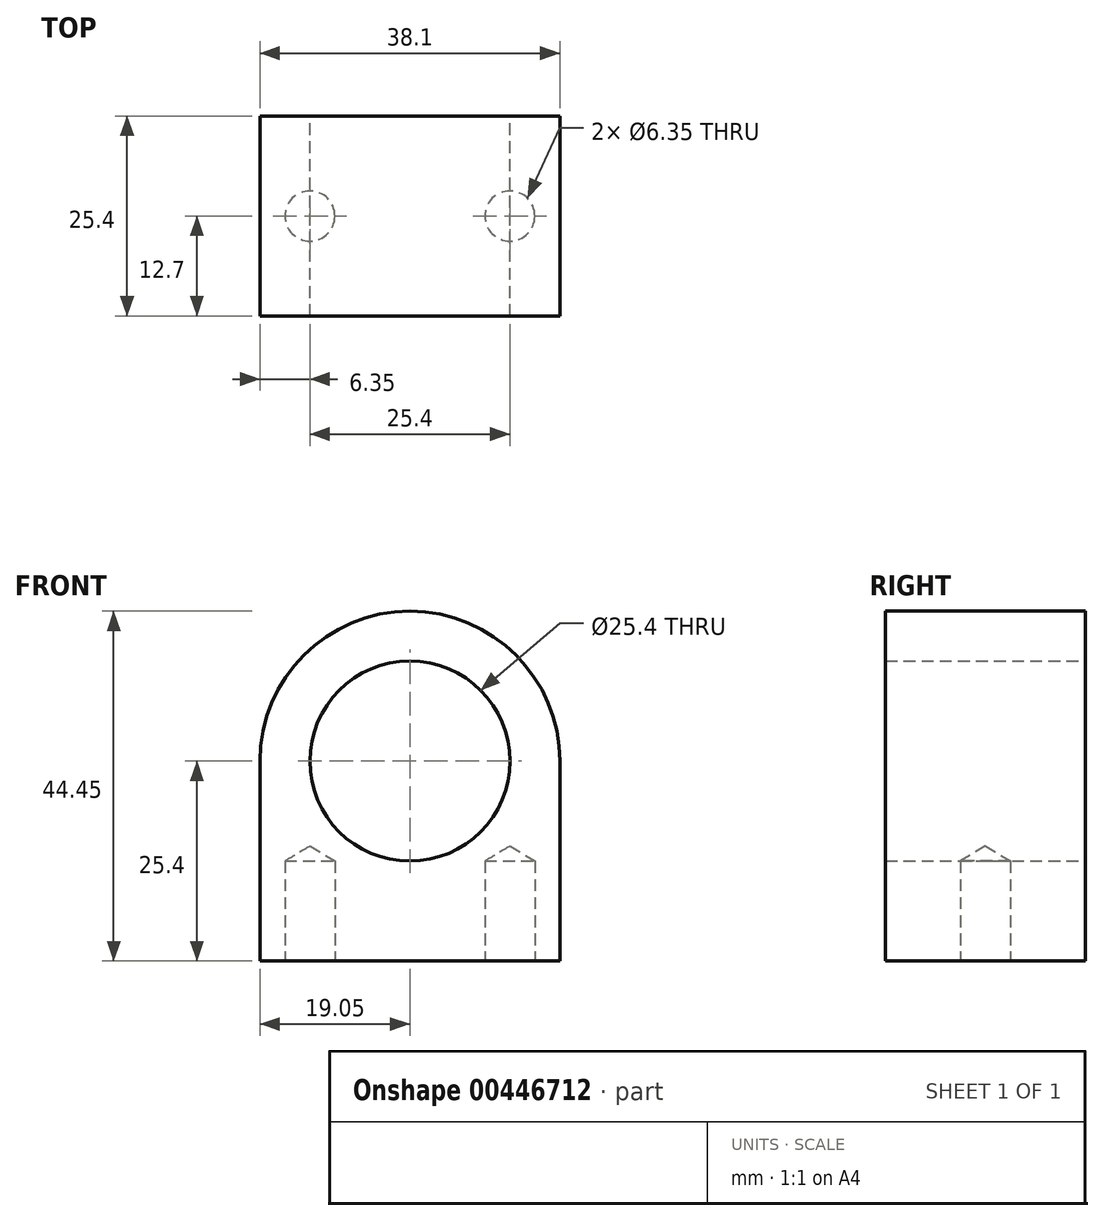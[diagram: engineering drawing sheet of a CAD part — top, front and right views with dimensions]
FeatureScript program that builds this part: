
annotation { "Feature Type Name" : "Feature", "Feature Type Description" : "" }
export const myFeature = defineFeature(function(context is Context, id is Id, definition is map)
    precondition{}
    {
        {
            var Q0;
            Q0=qCreatedBy(makeId("Front.planeOp"),FACE);
            var sketch = newSketch(context, id + "F0", { "sketchPlane" : qUnion([Q0])});
            skArc(sketch, "E0", {"start": v(19.05, 0) * mm, "mid": v(0, 19.05) * mm, "end": v(-19.05, 0) * mm});
            skCircle(sketch, "E1", {"center": v(0, 0) * mm, "radius": 12.7 * mm});
            skLineSegment(sketch, "E2", {"start": v(-19.05, 0) * mm, "end": v(-19.05, -25.4) * mm});
            skLineSegment(sketch, "E3", {"start": v(-19.05, -25.4) * mm, "end": v(19.05, -25.4) * mm});
            skLineSegment(sketch, "E4", {"start": v(19.05, 0) * mm, "end": v(19.05, -25.4) * mm});
            skSolve(sketch);
        }
        {
            var Q0;
            Q0=makeQuery(id+"F0.imprint","IMPRINT",FACE,{"disambiguationData":[TD([[makeQuery(id+"F0.imprint","IMPRINT",EDGE,{"derivedFrom":sQuery(id+"F0.wireOp",EDGE,"E0")}),1.0]])]});
            extrude(context, id + "F1", {"entities" : qUnion([Q0]), "depth" : 25.4 * mm});
        }
        {
            var Q0;
            Q0=makeQuery(id+"F1.opExtrude","SWEPT_FACE",FACE,{"disambiguationData":[OSD([sQuery(id+"F0.wireOp",EDGE,"E3")])]});
            var sketch = newSketch(context, id + "F2", { "sketchPlane" : qUnion([Q0])});
            skPoint(sketch, "E5", {"position": v(-12.7, 12.7) * mm});
            skPoint(sketch, "E6", {"position": v(12.7, 12.7) * mm});
            skSolve(sketch);
        }
        {
            var Q0;
            Q0=sQuery(id+"F2.wireOp",VERTEX,"E5");
            var Q1;
            Q1=sQuery(id+"F2.wireOp",VERTEX,"E6");
            var Q2;
            Q2=makeQuery(id+"F1.opExtrude","SWEPT_BODY",BODY,{"disambiguationData":[OSD([sQuery(id+"F0.wireOp",EDGE,"E0"),sQuery(id+"F0.wireOp",EDGE,"E1"),sQuery(id+"F0.wireOp",EDGE,"E2"),sQuery(id+"F0.wireOp",EDGE,"E3"),sQuery(id+"F0.wireOp",EDGE,"E4")])]});
            hole(context, id + "F3", {"style" : HoleStyle.SIMPLE, "endStyle" : HoleEndStyle.BLIND, "holeDiameter" : 6.35 * mm, "holeDepth" : 12.7 * mm, "isTappedThrough" : true, "tappedDepth" : 12.7 * mm, "tapClearance" : 3, "locations" : qUnion([Q0, Q1]), "scope" : qUnion([Q2])});
        }
    });
